# Revit family: SLIM_255x150x7.8
name_source: partatom
category: Plumbing Fixtures
revit_build: Autodesk Revit 2018 (Build: 20170223_1515(x64)
units: mm (PartAtom-declared; Revit-internal decimal feet)

## family parameters
Always vertical = Yes
Cut with Voids When Loaded = No
OmniClass Number = 23.45.00.00
OmniClass Title = Sanitary, Laundry, and Cleaning Equipment
Part Type = Normal
Room Calculation Point = No
Round Connector Dimension = Use Diameter
Shared = No
Work Plane-Based = Yes

## types (1)
- Mécanique_Inox brossé
    BIM object developer = www.concepsysbim.com
    CONTROL_Actuation type = Mécanique
    CONTROL_Brief description = Gracieusement unique
    CONTROL_Height = 150 mm
    CONTROL_Length = 255 mm  [stored 0.836614 ft]
    CONTROL_Material = Inox brossé
    CONTROL_Model = SLIM CASINO INOX
    CONTROL_Model Series = Inox brossé
    CONTROL_Model code/ref = 173 i
    CONTROL_Product data url = https://www.regiplast.fr
    CONTROL_Type of flush = Double-Débit
    CONTROL_Type/function = Plaque de Commande pour réservoir à encastrer
    CONTROL_Width = 7.8 mm  [stored 0.0255906 ft]
    Default Elevation = 1219.2 mm  [stored 4 ft]
    Description = Gracieusement unique
    HORIZONTAL = No
    Model = SLIM CASINO INOX
    Product data url = https://www.regiplast.fr
    URL = https://www.regiplast.fr
    VERTICAL = Yes

note: [stored X ft] marks values corroborated as IEEE doubles in the binary element streams (Revit-internal decimal feet)

## geometry (parser evidence)
native form markers: Sweep x9
no freeform markers — native parametric forms only
